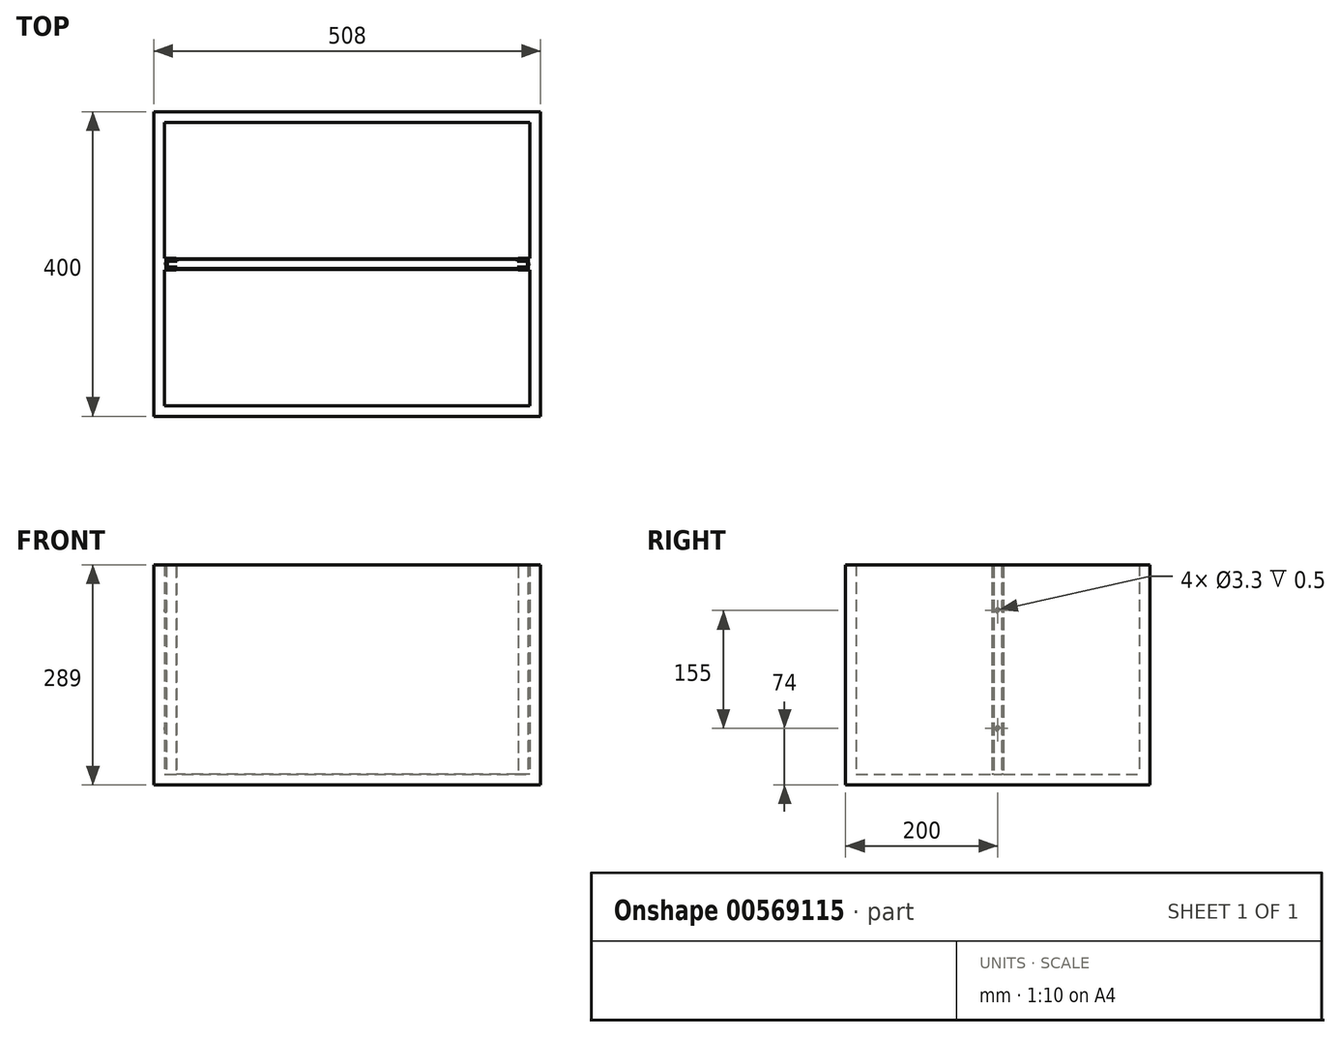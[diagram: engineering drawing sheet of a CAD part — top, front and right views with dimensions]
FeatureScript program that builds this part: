
annotation { "Feature Type Name" : "Feature", "Feature Type Description" : "" }
export const myFeature = defineFeature(function(context is Context, id is Id, definition is map)
    precondition{}
    {
        {
            var Q0;
            Q0=qCreatedBy(makeId("Top.planeOp"),FACE);
            var sketch = newSketch(context, id + "F0", { "sketchPlane" : qUnion([Q0])});
            skLineSegment(sketch, "E0.bottom", {"start": v(-240, -7.5) * mm, "end": v(-225, -7.5) * mm});
            skLineSegment(sketch, "E0.top", {"start": v(-240, 7.5) * mm, "end": v(-225, 7.5) * mm});
            skLineSegment(sketch, "E0.left", {"start": v(-240, -7.5) * mm, "end": v(-240, 7.5) * mm});
            skPoint(sketch, "E0.middle", {"position": v(-232.5, 0) * mm});
            skLineSegment(sketch, "E1.0", {"start": v(-238, 5.5) * mm, "end": v(-225, 5.5) * mm});
            skLineSegment(sketch, "E1.1", {"start": v(-238, -5.5) * mm, "end": v(-238, 5.5) * mm});
            skLineSegment(sketch, "E1.2", {"start": v(-238, -5.5) * mm, "end": v(-225, -5.5) * mm});
            skLineSegment(sketch, "E2", {"start": v(-225, 7.5) * mm, "end": v(-225, 5.5) * mm});
            skLineSegment(sketch, "E3", {"start": v(-225, -5.5) * mm, "end": v(-225, -7.5) * mm});
            skLineSegment(sketch, "E4", {"start": v(0, 11.48) * mm, "end": v(0, -13.1) * mm, "construction": true});
            skSolve(sketch);
        }
        {
            var Q0;
            Q0 = qSketchRegion(id + "F0", true);
            extrude(context, id + "F1", {"entities" : qUnion([Q0]), "depth" : 275 * mm, "offsetDistance" : 25 * mm});
        }
        {
            var Q0;
            Q0=makeQuery(id+"F1.opExtrude","CAP_EDGE",EDGE,{"disambiguationData":[OSD([sQuery(id+"F0.wireOp",EDGE,"E3")])],"isStart":false});
            var Q1;
            Q1=makeQuery(id+"F1.opExtrude","CAP_EDGE",EDGE,{"disambiguationData":[OSD([sQuery(id+"F0.wireOp",EDGE,"E2")])],"isStart":false});
            fillet(context, id + "F2", {"entities" : qUnion([Q0, Q1]), "radius" : 2 * mm, "tangentPropagation" : true, "allowEdgeOverflow" : false});
        }
        {
            var Q0;
            Q0=makeQuery(id+"F1.opExtrude","SWEPT_FACE",FACE,{"disambiguationData":[OSD([sQuery(id+"F0.wireOp",EDGE,"E1.1")])]});
            var sketch = newSketch(context, id + "F3", { "sketchPlane" : qUnion([Q0])});
            skLineSegment(sketch, "E5", {"start": v(0, 60) * mm, "end": v(0, 215) * mm, "construction": true});
            skSolve(sketch);
        }
        {
            var Q0;
            Q0=sQuery(id+"F3.wireOp",VERTEX,"E5.end");
            var Q1;
            Q1=sQuery(id+"F3.wireOp",VERTEX,"E5.start");
            var Q2;
            Q2=makeQuery(id+"F1.opExtrude","SWEPT_BODY",BODY,{"disambiguationData":[OSD([sQuery(id+"F0.wireOp",EDGE,"E0.bottom"),sQuery(id+"F0.wireOp",EDGE,"E0.top"),sQuery(id+"F0.wireOp",EDGE,"E0.left"),sQuery(id+"F0.wireOp",EDGE,"E1.0"),sQuery(id+"F0.wireOp",EDGE,"E1.1"),sQuery(id+"F0.wireOp",EDGE,"E1.2"),sQuery(id+"F0.wireOp",EDGE,"E2"),sQuery(id+"F0.wireOp",EDGE,"E3")])]});
            hole(context, id + "F4", {"style" : HoleStyle.C_SINK, "endStyle" : HoleEndStyle.THROUGH, "holeDiameter" : 3.3 * mm, "cSinkDiameter" : 6.3 * mm, "cSinkAngle" : 90 * degree, "isTappedThrough" : true, "tappedDepth" : 12 * mm, "tapClearance" : 3, "locations" : qUnion([Q0, Q1]), "scope" : qUnion([Q2])});
        }
        {
            var Q0;
            Q0=makeQuery(id+"F1.opExtrude","SWEPT_BODY",BODY,{"disambiguationData":[OSD([sQuery(id+"F0.wireOp",EDGE,"E0.bottom"),sQuery(id+"F0.wireOp",EDGE,"E0.top"),sQuery(id+"F0.wireOp",EDGE,"E0.left"),sQuery(id+"F0.wireOp",EDGE,"E1.0"),sQuery(id+"F0.wireOp",EDGE,"E1.1"),sQuery(id+"F0.wireOp",EDGE,"E1.2"),sQuery(id+"F0.wireOp",EDGE,"E2"),sQuery(id+"F0.wireOp",EDGE,"E3")])]});
            var Q1;
            Q1=qCreatedBy(makeId("Right.planeOp"),FACE);
            mirror(context, id + "F5", {"entities" : qUnion([Q0]), "mirrorPlane" : qUnion([Q1])});
        }
        {
            var Q0;
            Q0=qCreatedBy(makeId("Top.planeOp"),FACE);
            var sketch = newSketch(context, id + "F6", { "sketchPlane" : qUnion([Q0])});
            skLineSegment(sketch, "E6.bottom", {"start": v(-240, -186) * mm, "end": v(240, -186) * mm});
            skLineSegment(sketch, "E6.top", {"start": v(-240, 186) * mm, "end": v(240, 186) * mm});
            skLineSegment(sketch, "E6.left", {"start": v(-240, -186) * mm, "end": v(-240, 186) * mm});
            skLineSegment(sketch, "E6.right", {"start": v(240, -186) * mm, "end": v(240, 186) * mm});
            skPoint(sketch, "E6.middle", {"position": v(0, 0) * mm});
            skLineSegment(sketch, "E7.0", {"start": v(-254, 200) * mm, "end": v(254, 200) * mm});
            skLineSegment(sketch, "E7.1", {"start": v(-254, -200) * mm, "end": v(-254, 200) * mm});
            skLineSegment(sketch, "E7.2", {"start": v(-254, -200) * mm, "end": v(254, -200) * mm});
            skLineSegment(sketch, "E7.3", {"start": v(254, -200) * mm, "end": v(254, 200) * mm});
            skSolve(sketch);
        }
        {
            var Q0;
            Q0=makeQuery(id+"F6.imprint","IMPRINT",FACE,{"disambiguationData":[TD([[makeQuery(id+"F6.imprint","IMPRINT",EDGE,{"derivedFrom":sQuery(id+"F6.wireOp",EDGE,"E6.bottom")}),1.0]])]});
            var sketch = newSketch(context, id + "F7", { "sketchPlane" : qUnion([Q0])});
            skLineSegment(sketch, "E8", {"start": v(0, 19.65) * mm, "end": v(0, -26.6) * mm, "construction": true});
            skLineSegment(sketch, "E9.0", {"start": v(-224.5, -5) * mm, "end": v(-224.5, -7) * mm});
            skLineSegment(sketch, "E9.1", {"start": v(-224.5, 7) * mm, "end": v(-224.5, 5) * mm});
            skLineSegment(sketch, "E9.2", {"start": v(-237.5, 5) * mm, "end": v(-224.5, 5) * mm});
            skLineSegment(sketch, "E9.3", {"start": v(-237.5, -5) * mm, "end": v(-237.5, 5) * mm});
            skLineSegment(sketch, "E9.4", {"start": v(-237.5, -5) * mm, "end": v(-224.5, -5) * mm});
            skLineSegment(sketch, "E10.MirrorCS", {"start": v(224.5, -5) * mm, "end": v(224.5, -7) * mm});
            skLineSegment(sketch, "E11.MirrorCS", {"start": v(224.5, 7) * mm, "end": v(224.5, 5) * mm});
            skLineSegment(sketch, "E12.MirrorCS", {"start": v(237.5, -5) * mm, "end": v(237.5, 5) * mm});
            skLineSegment(sketch, "E13.MirrorCS", {"start": v(237.5, -5) * mm, "end": v(224.5, -5) * mm});
            skLineSegment(sketch, "E14.MirrorCS", {"start": v(237.5, 5) * mm, "end": v(224.5, 5) * mm});
            skLineSegment(sketch, "E15", {"start": v(-224.5, 7) * mm, "end": v(224.5, 7) * mm});
            skLineSegment(sketch, "E16", {"start": v(224.5, -7) * mm, "end": v(-224.5, -7) * mm});
            skLineSegment(sketch, "E17", {"start": v(-237.5, 0) * mm, "end": v(237.5, 0) * mm, "construction": true});
            skSolve(sketch);
        }
        {
            var Q0;
            Q0 = qSketchRegion(id + "F7", true);
            var Q1;
            Q1=makeQuery(id+"F1.opExtrude","CAP_VERTEX",VERTEX,{"disambiguationData":[OSD([sQuery(id+"F0.wireOp",EDGE,"E1.1"),sQuery(id+"F0.wireOp",EDGE,"E1.2")])],"isStart":false});
            extrude(context, id + "F8", {"entities" : qUnion([Q0]), "endBound" : BoundingType.UP_TO_VERTEX, "depth" : 25 * mm, "endBoundEntityVertex" : qUnion([Q1]), "offsetDistance" : 25 * mm});
        }
        {
            var Q0;
            Q0=makeQuery(id+"F8.opExtrude","CAP_EDGE",EDGE,{"disambiguationData":[OSD([sQuery(id+"F7.wireOp",EDGE,"E16")])],"isStart":false});
            var Q1;
            Q1=makeQuery(id+"F8.opExtrude","CAP_EDGE",EDGE,{"disambiguationData":[OSD([sQuery(id+"F7.wireOp",EDGE,"E15")])],"isStart":false});
            var Q2;
            Q2=makeQuery(id+"F8.opExtrude","CAP_EDGE",EDGE,{"disambiguationData":[OSD([sQuery(id+"F7.wireOp",EDGE,"E9.0")])],"isStart":false});
            var Q3;
            Q3=makeQuery(id+"F8.opExtrude","CAP_EDGE",EDGE,{"disambiguationData":[OSD([sQuery(id+"F7.wireOp",EDGE,"E9.4")])],"isStart":false});
            var Q4;
            Q4=makeQuery(id+"F8.opExtrude","CAP_EDGE",EDGE,{"disambiguationData":[OSD([sQuery(id+"F7.wireOp",EDGE,"E9.3")])],"isStart":false});
            var Q5;
            Q5=makeQuery(id+"F8.opExtrude","CAP_EDGE",EDGE,{"disambiguationData":[OSD([sQuery(id+"F7.wireOp",EDGE,"E9.1")])],"isStart":false});
            var Q6;
            Q6=makeQuery(id+"F8.opExtrude","CAP_EDGE",EDGE,{"disambiguationData":[OSD([sQuery(id+"F7.wireOp",EDGE,"E9.2")])],"isStart":false});
            var Q7;
            Q7=makeQuery(id+"F8.opExtrude","CAP_EDGE",EDGE,{"disambiguationData":[OSD([sQuery(id+"F7.wireOp",EDGE,"E11.MirrorCS")])],"isStart":false});
            var Q8;
            Q8=makeQuery(id+"F8.opExtrude","CAP_EDGE",EDGE,{"disambiguationData":[OSD([sQuery(id+"F7.wireOp",EDGE,"E10.MirrorCS")])],"isStart":false});
            var Q9;
            Q9=makeQuery(id+"F8.opExtrude","CAP_EDGE",EDGE,{"disambiguationData":[OSD([sQuery(id+"F7.wireOp",EDGE,"E13.MirrorCS")])],"isStart":false});
            var Q10;
            Q10=makeQuery(id+"F8.opExtrude","CAP_EDGE",EDGE,{"disambiguationData":[OSD([sQuery(id+"F7.wireOp",EDGE,"E14.MirrorCS")])],"isStart":false});
            var Q11;
            Q11=makeQuery(id+"F8.opExtrude","CAP_EDGE",EDGE,{"disambiguationData":[OSD([sQuery(id+"F7.wireOp",EDGE,"E12.MirrorCS")])],"isStart":false});
            chamfer(context, id + "F9", {"entities" : qUnion([Q0, Q1, Q2, Q3, Q4, Q5, Q6, Q7, Q8, Q9, Q10, Q11]), "width" : 1 * mm, "tangentPropagation" : true});
        }
        {
            var Q0;
            Q0=makeQuery(id+"F6.imprint","IMPRINT",FACE,{"disambiguationData":[TD([[makeQuery(id+"F6.imprint","IMPRINT",EDGE,{"derivedFrom":sQuery(id+"F6.wireOp",EDGE,"E6.bottom")}),-1.0]])]});
            var Q1;
            Q1=makeQuery(id+"F1.opExtrude","CAP_VERTEX",VERTEX,{"disambiguationData":[OSD([sQuery(id+"F0.wireOp",EDGE,"E0.bottom"),sQuery(id+"F0.wireOp",EDGE,"E0.left")])],"isStart":false});
            extrude(context, id + "F10", {"entities" : qUnion([Q0]), "endBound" : BoundingType.UP_TO_VERTEX, "depth" : 25 * mm, "endBoundEntityVertex" : qUnion([Q1]), "offsetDistance" : 25 * mm});
        }
        {
            var Q0;
            Q0=makeQuery(id+"F10.opExtrude","CAP_FACE",FACE,{"disambiguationData":[OSD([sQuery(id+"F6.wireOp",EDGE,"E6.bottom"),sQuery(id+"F6.wireOp",EDGE,"E6.top"),sQuery(id+"F6.wireOp",EDGE,"E6.left"),sQuery(id+"F6.wireOp",EDGE,"E6.right"),sQuery(id+"F6.wireOp",EDGE,"E7.0"),sQuery(id+"F6.wireOp",EDGE,"E7.1"),sQuery(id+"F6.wireOp",EDGE,"E7.2"),sQuery(id+"F6.wireOp",EDGE,"E7.3")])],"isStart":true});
            var sketch = newSketch(context, id + "F11", { "sketchPlane" : qUnion([Q0])});
            skLineSegment(sketch, "E18.0", {"start": v(-254, 200) * mm, "end": v(-254, -200) * mm});
            skLineSegment(sketch, "E18.1", {"start": v(-254, 200) * mm, "end": v(254, 200) * mm});
            skLineSegment(sketch, "E18.2", {"start": v(254, 200) * mm, "end": v(254, -200) * mm});
            skLineSegment(sketch, "E18.3", {"start": v(-254, -200) * mm, "end": v(254, -200) * mm});
            skSolve(sketch);
        }
        {
            var Q0;
            Q0 = qSketchRegion(id + "F11", true);
            extrude(context, id + "F12", {"entities" : qUnion([Q0]), "operationType" : NewBodyOperationType.ADD, "depth" : 14 * mm, "offsetDistance" : 25 * mm});
        }
    });
